FCSTD DOCUMENT  (FreeCAD 0.18.4R)
Label: nugget-2.0-outline
License: All rights reserved
LicenseURL: http://en.wikipedia.org/wiki/All_rights_reserved
objects: Sketcher::SketchObject×1
note: 1 computed .brp shape members not serialized (recipe doc carries the construction recipe); baked Part::Feature solids carry a one-line shape summary decoded from their .brp

FEATURE [Sketcher::SketchObject] Sketch
  sketch-geometry (10):
    g0: LineSegment StartX=-21 StartY=20 StartZ=0 EndX=-13.75 EndY=31 EndZ=0
    g1: LineSegment StartX=-13.75 StartY=31 StartZ=0 EndX=-6.5 EndY=20 EndZ=0
    g2: LineSegment StartX=-6.5 StartY=20 StartZ=0 EndX=6.5 EndY=20 EndZ=0
    g3: LineSegment StartX=6.5 StartY=20 StartZ=0 EndX=13.75 EndY=31 EndZ=0
    g4: LineSegment StartX=13.75 StartY=31 StartZ=0 EndX=21 EndY=20 EndZ=0
    g5: LineSegment StartX=21 StartY=20 StartZ=0 EndX=21 EndY=-20 EndZ=0
    g6: LineSegment StartX=21 StartY=-20 StartZ=0 EndX=12.7 EndY=-28 EndZ=0
    g7: LineSegment StartX=12.7 StartY=-28 StartZ=0 EndX=-12.7 EndY=-28 EndZ=0
    g8: LineSegment StartX=-12.7 StartY=-28 StartZ=0 EndX=-21 EndY=-20 EndZ=0
    g9: LineSegment StartX=-21 StartY=-20 StartZ=0 EndX=-21 EndY=20 EndZ=0
  constraints (26):
    c: Coincident(g0,g1)
    c: Coincident(g1,g2)
    c: Coincident(g2,g3)
    c: Coincident(g3,g4)
    c: Coincident(g4,g5)
    c: Vertical(g5)
    c: Coincident(g5,g6)
    c: Coincident(g6,g7)
    c: Coincident(g7,g8)
    c: Coincident(g8,g9)
    c: Coincident(g9,g0)
    c: DistanceY(g9,g9) = 40
    c: DistanceY(g7,g0) = 59
    c: DistanceY(g6,g5) = 8
    c: DistanceX(g2,g2) = 13
    c: DistanceX(g6,g5) = 8.3
    c: Equal(g5,g9)
    c: Equal(g0,g1)
    c: Equal(g1,g3)
    c: Equal(g3,g4)
    c: Symmetric(g2,g1,g-2)
    c: Symmetric(g7,g6,g-2)
    c: Symmetric(g0,g4,g-2)
    c: Horizontal(g2,g4)
    c: DistanceX(g8,g5) = 42
    c: Symmetric(g0,g8,g-1)
